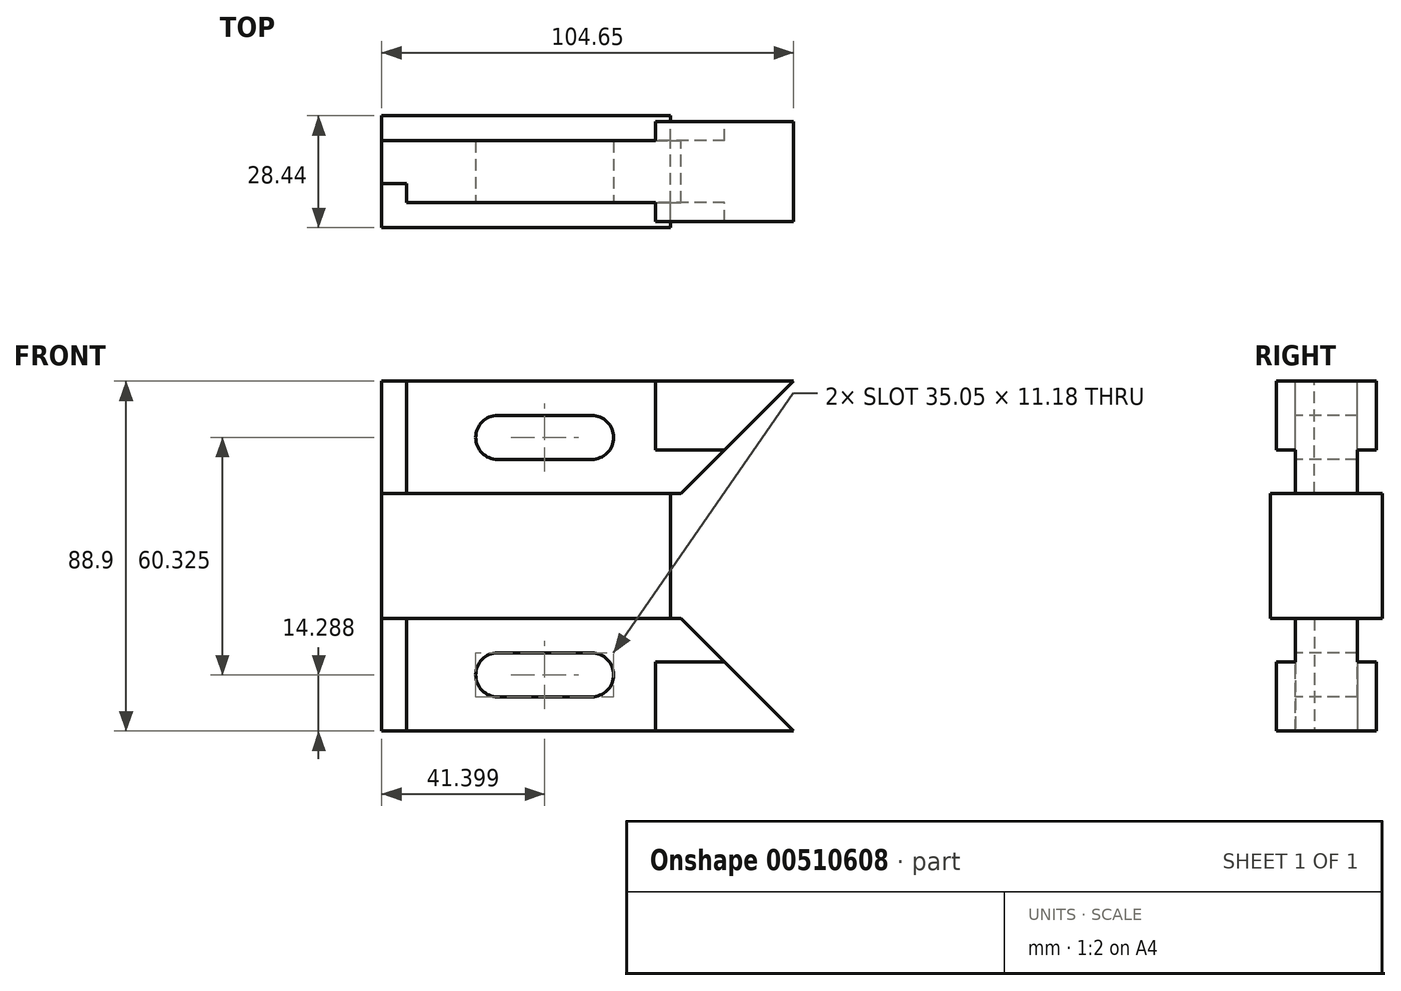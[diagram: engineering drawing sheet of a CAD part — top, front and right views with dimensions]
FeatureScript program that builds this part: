
annotation { "Feature Type Name" : "Feature", "Feature Type Description" : "" }
export const myFeature = defineFeature(function(context is Context, id is Id, definition is map)
    precondition{}
    {
        {
            var Q0;
            Q0=qCreatedBy(makeId("Front.planeOp"),FACE);
            var sketch = newSketch(context, id + "F0", { "sketchPlane" : qUnion([Q0])});
            skLineSegment(sketch, "E0.bottom", {"start": v(-36.7, 15.88) * mm, "end": v(36.7, 15.88) * mm});
            skLineSegment(sketch, "E0.top", {"start": v(-36.7, -15.88) * mm, "end": v(36.7, -15.88) * mm});
            skLineSegment(sketch, "E0.left", {"start": v(-36.7, 15.88) * mm, "end": v(-36.7, -15.88) * mm});
            skLineSegment(sketch, "E0.right", {"start": v(36.7, 15.88) * mm, "end": v(36.7, -15.88) * mm});
            skPoint(sketch, "E0.middle", {"position": v(0, 0) * mm});
            skLineSegment(sketch, "E1", {"start": v(-36.7, 15.88) * mm, "end": v(-36.7, 44.45) * mm});
            skLineSegment(sketch, "E2", {"start": v(-36.7, 44.45) * mm, "end": v(67.95, 44.45) * mm});
            skLineSegment(sketch, "E3", {"start": v(67.95, 44.45) * mm, "end": v(39.37, 15.87) * mm});
            skLineSegment(sketch, "E4.MirrorCS", {"start": v(-36.7, -15.88) * mm, "end": v(-36.7, -44.45) * mm});
            skLineSegment(sketch, "E5.MirrorCS", {"start": v(-36.7, -44.45) * mm, "end": v(67.95, -44.45) * mm});
            skLineSegment(sketch, "E6.MirrorCS", {"start": v(67.95, -44.45) * mm, "end": v(39.37, -15.87) * mm});
            skPoint(sketch, "E7.end.orphan", {"position": v(36.7, -15.88) * mm});
            skLineSegment(sketch, "E8", {"start": v(36.7, 15.88) * mm, "end": v(39.37, 15.88) * mm});
            skLineSegment(sketch, "E9", {"start": v(39.37, -15.88) * mm, "end": v(36.7, -15.88) * mm});
            skSolve(sketch);
        }
        {
            var Q0;
            Q0=qCreatedBy(makeId("Front.planeOp"),FACE);
            var sketch = newSketch(context, id + "F1", { "sketchPlane" : qUnion([Q0])});
            skLineSegment(sketch, "E10.bottom", {"start": v(16.64, 35.75) * mm, "end": v(-7.24, 35.75) * mm});
            skLineSegment(sketch, "E10.top", {"start": v(16.64, 24.57) * mm, "end": v(-7.24, 24.57) * mm});
            skPoint(sketch, "E10.middle", {"position": v(4.7, 30.16) * mm});
            skArc(sketch, "E11", {"start": v(-7.24, 35.75) * mm, "mid": v(-12.83, 30.16) * mm, "end": v(-7.24, 24.57) * mm});
            skArc(sketch, "E12", {"start": v(16.64, 24.57) * mm, "mid": v(22.22, 30.16) * mm, "end": v(16.64, 35.75) * mm});
            skLineSegment(sketch, "E13.MirrorCS", {"start": v(16.64, -35.75) * mm, "end": v(-7.24, -35.75) * mm});
            skLineSegment(sketch, "E14.MirrorCS", {"start": v(16.64, -24.57) * mm, "end": v(-7.24, -24.57) * mm});
            skArc(sketch, "E15.MirrorCS", {"start": v(16.64, -24.57) * mm, "mid": v(22.22, -30.16) * mm, "end": v(16.64, -35.75) * mm});
            skPoint(sketch, "E16.MirrorP", {"position": v(4.7, -30.16) * mm});
            skArc(sketch, "E17.MirrorCS", {"start": v(-7.24, -35.75) * mm, "mid": v(-12.83, -30.16) * mm, "end": v(-7.24, -24.57) * mm});
            skCircle(sketch, "E18", {"center": v(-7.24, -30.16) * mm, "radius": 14.29 * mm, "construction": true});
            skCircle(sketch, "E19.MirrorC", {"center": v(-7.24, 30.16) * mm, "radius": 14.29 * mm, "construction": true});
            skPoint(sketch, "E20.orphan", {"position": v(11.12, 29.27) * mm});
            skPoint(sketch, "E21.orphan", {"position": v(11.12, -29.27) * mm});
            skSolve(sketch);
        }
        {
            var Q0;
            Q0=qCreatedBy(makeId("Front.planeOp"),FACE);
            var sketch = newSketch(context, id + "F2", { "sketchPlane" : qUnion([Q0])});
            skLineSegment(sketch, "E22.0", {"start": v(32.9, 44.45) * mm, "end": v(67.95, 44.45) * mm});
            skLineSegment(sketch, "E23.0", {"start": v(67.95, 44.45) * mm, "end": v(50.42, 26.92) * mm});
            skLineSegment(sketch, "E24.0", {"start": v(67.95, -44.45) * mm, "end": v(50.42, -26.92) * mm});
            skLineSegment(sketch, "E25.0", {"start": v(32.9, -44.45) * mm, "end": v(67.95, -44.45) * mm});
            skLineSegment(sketch, "E26", {"start": v(32.9, 44.45) * mm, "end": v(32.9, 26.92) * mm});
            skLineSegment(sketch, "E27", {"start": v(32.9, 26.92) * mm, "end": v(50.42, 26.92) * mm});
            skLineSegment(sketch, "E28.MirrorCS", {"start": v(32.9, -44.45) * mm, "end": v(32.9, -26.92) * mm});
            skLineSegment(sketch, "E29.MirrorCS", {"start": v(32.9, -26.92) * mm, "end": v(50.42, -26.92) * mm});
            skPoint(sketch, "E30.orphan", {"position": v(-36.7, 44.45) * mm});
            skPoint(sketch, "E31.orphan", {"position": v(39.37, 15.87) * mm});
            skPoint(sketch, "E32.orphan", {"position": v(39.37, -15.87) * mm});
            skPoint(sketch, "E33.orphan", {"position": v(-36.7, -44.45) * mm});
            skSolve(sketch);
        }
        {
            var Q0;
            Q0=qCreatedBy(makeId("Right.planeOp"),FACE);
            var sketch = newSketch(context, id + "F3", { "sketchPlane" : qUnion([Q0])});
            skLineSegment(sketch, "E34.bottom", {"start": v(14.22, 15.88) * mm, "end": v(-14.22, 15.88) * mm});
            skLineSegment(sketch, "E34.top", {"start": v(14.22, -15.88) * mm, "end": v(-14.22, -15.88) * mm});
            skLineSegment(sketch, "E34.left", {"start": v(14.22, 15.88) * mm, "end": v(14.22, -15.88) * mm});
            skLineSegment(sketch, "E34.right", {"start": v(-14.22, 15.88) * mm, "end": v(-14.22, -15.88) * mm});
            skPoint(sketch, "E34.middle", {"position": v(0, 0) * mm});
            skLineSegment(sketch, "E35.bottom", {"start": v(12.7, 44.45) * mm, "end": v(-12.7, 44.45) * mm});
            skLineSegment(sketch, "E35.top", {"start": v(12.7, 26.92) * mm, "end": v(-12.7, 26.92) * mm});
            skLineSegment(sketch, "E35.left", {"start": v(12.7, 44.45) * mm, "end": v(12.7, 26.92) * mm});
            skLineSegment(sketch, "E35.right", {"start": v(-12.7, 44.45) * mm, "end": v(-12.7, 26.92) * mm});
            skPoint(sketch, "E35.middle", {"position": v(0, 35.69) * mm});
            skLineSegment(sketch, "E36", {"start": v(-7.87, 44.45) * mm, "end": v(-7.87, 15.88) * mm});
            skLineSegment(sketch, "E37", {"start": v(-3.05, 44.45) * mm, "end": v(-3.05, 15.88) * mm});
            skLineSegment(sketch, "E38.MirrorCS", {"start": v(7.87, 44.45) * mm, "end": v(7.87, 15.88) * mm});
            skSolve(sketch);
        }
        {
            var Q0;
            Q0=sQuery(id+"F3.wireOp",EDGE,"E37");
            cPlane(context, id + "F4", {"entities" : qUnion([Q0]), "cplaneType" : CPlaneType.LINE_ANGLE, "offset" : 25.4 * mm, "angle" : 90 * degree, "oppositeDirection" : true, "width" : 152.4 * mm, "height" : 152.4 * mm});
        }
        {
            var Q0;
            Q0=qCreatedBy(id+"F4.planeOp",FACE);
            var sketch = newSketch(context, id + "F5", { "sketchPlane" : qUnion([Q0])});
            skLineSegment(sketch, "E39.0", {"start": v(-36.7, 15.88) * mm, "end": v(-36.7, 44.45) * mm});
            skLineSegment(sketch, "E40.0", {"start": v(-36.7, 44.45) * mm, "end": v(-30.35, 44.45) * mm});
            skLineSegment(sketch, "E41.0", {"start": v(-36.7, 15.88) * mm, "end": v(-30.35, 15.88) * mm});
            skLineSegment(sketch, "E42.0", {"start": v(-36.7, -15.88) * mm, "end": v(-30.35, -15.88) * mm});
            skLineSegment(sketch, "E43.0", {"start": v(-36.7, -15.88) * mm, "end": v(-36.7, -44.45) * mm});
            skLineSegment(sketch, "E44.0", {"start": v(-36.7, -44.45) * mm, "end": v(-30.35, -44.45) * mm});
            skLineSegment(sketch, "E45", {"start": v(-30.35, 44.45) * mm, "end": v(-30.35, 15.88) * mm});
            skPoint(sketch, "E46.orphan", {"position": v(67.95, 44.45) * mm});
            skPoint(sketch, "E47.orphan", {"position": v(36.7, 15.88) * mm});
            skLineSegment(sketch, "E48.trimOffspring", {"start": v(-30.35, -15.88) * mm, "end": v(-30.35, -44.45) * mm});
            skPoint(sketch, "E49.orphan", {"position": v(36.7, -15.88) * mm});
            skPoint(sketch, "E50.orphan", {"position": v(67.95, -44.45) * mm});
            skSolve(sketch);
        }
        {
            var Q0;
            Q0=makeQuery(id+"F0.imprint","IMPRINT",FACE,{"disambiguationData":[TD([[makeQuery(id+"F0.imprint","IMPRINT",EDGE,{"derivedFrom":sQuery(id+"F0.wireOp",EDGE,"E0.bottom")}),-1.0]])]});
            var Q1;
            Q1=sQuery(id+"F3.wireOp",VERTEX,"E34.right.end");
            var Q2;
            Q2=sQuery(id+"F3.wireOp",VERTEX,"E34.left.start");
            extrude(context, id + "F6", {"entities" : qUnion([Q0]), "endBound" : BoundingType.UP_TO_VERTEX, "endBoundEntityVertex" : qUnion([Q1]), "depth" : 25.4 * mm, "hasSecondDirection" : true, "secondDirectionBound" : SecondDirectionBoundingType.UP_TO_VERTEX, "secondDirectionOppositeDirection" : true, "secondDirectionBoundEntityVertex" : qUnion([Q2]), "secondDirectionDepth" : 25.4 * mm});
        }
        {
            var Q0;
            Q0=makeQuery(id+"F0.imprint","IMPRINT",FACE,{"disambiguationData":[TD([[makeQuery(id+"F0.imprint","IMPRINT",EDGE,{"derivedFrom":sQuery(id+"F0.wireOp",EDGE,"E0.bottom")}),1.0]])]});
            var Q1;
            Q1=makeQuery(id+"F0.imprint","IMPRINT",FACE,{"disambiguationData":[TD([[makeQuery(id+"F0.imprint","IMPRINT",EDGE,{"derivedFrom":sQuery(id+"F0.wireOp",EDGE,"E0.top")}),-1.0]])]});
            var Q2;
            Q2=sQuery(id+"F3.wireOp",VERTEX,"E36.start");
            var Q3;
            Q3=sQuery(id+"F3.wireOp",VERTEX,"E38.MirrorCS.start");
            extrude(context, id + "F7", {"entities" : qUnion([Q0, Q1]), "operationType" : NewBodyOperationType.ADD, "endBound" : BoundingType.UP_TO_VERTEX, "endBoundEntityVertex" : qUnion([Q2]), "depth" : 25.4 * mm, "hasSecondDirection" : true, "secondDirectionBound" : SecondDirectionBoundingType.UP_TO_VERTEX, "secondDirectionOppositeDirection" : true, "secondDirectionBoundEntityVertex" : qUnion([Q3]), "secondDirectionDepth" : 25.4 * mm});
        }
        {
            var Q0;
            Q0=qSketchRegion(id+"F1",true);
            var Q1;
            Q1=sQuery(id+"F3.wireOp",VERTEX,"E35.left.start");
            var Q2;
            Q2=sQuery(id+"F3.wireOp",VERTEX,"E35.bottom.end");
            extrude(context, id + "F8", {"entities" : qUnion([Q0]), "operationType" : NewBodyOperationType.REMOVE, "endBound" : BoundingType.UP_TO_VERTEX, "oppositeDirection" : true, "endBoundEntityVertex" : qUnion([Q1]), "depth" : 25.4 * mm, "hasSecondDirection" : true, "secondDirectionBound" : SecondDirectionBoundingType.UP_TO_VERTEX, "secondDirectionOppositeDirection" : false, "secondDirectionBoundEntityVertex" : qUnion([Q2]), "secondDirectionDepth" : 25.4 * mm});
        }
        {
            var Q0;
            Q0=qSketchRegion(id+"F2",true);
            var Q1;
            Q1=sQuery(id+"F3.wireOp",VERTEX,"E35.bottom.end");
            var Q2;
            Q2=sQuery(id+"F3.wireOp",VERTEX,"E35.left.start");
            extrude(context, id + "F9", {"entities" : qUnion([Q0]), "operationType" : NewBodyOperationType.ADD, "endBound" : BoundingType.UP_TO_VERTEX, "endBoundEntityVertex" : qUnion([Q1]), "depth" : 25.4 * mm, "hasSecondDirection" : true, "secondDirectionBound" : SecondDirectionBoundingType.UP_TO_VERTEX, "secondDirectionOppositeDirection" : true, "secondDirectionBoundEntityVertex" : qUnion([Q2]), "secondDirectionDepth" : 25.4 * mm});
        }
        {
            var Q0;
            Q0=qSketchRegion(id+"F5",true);
            var Q1;
            Q1=sQuery(id+"F3.wireOp",VERTEX,"E35.bottom.end");
            var Q2;
            Q2=sQuery(id+"F3.wireOp",VERTEX,"E37.start");
            extrude(context, id + "F10", {"entities" : qUnion([Q0]), "operationType" : NewBodyOperationType.REMOVE, "endBound" : BoundingType.UP_TO_VERTEX, "endBoundEntityVertex" : qUnion([Q1]), "depth" : 25.4 * mm});
        }
    });
